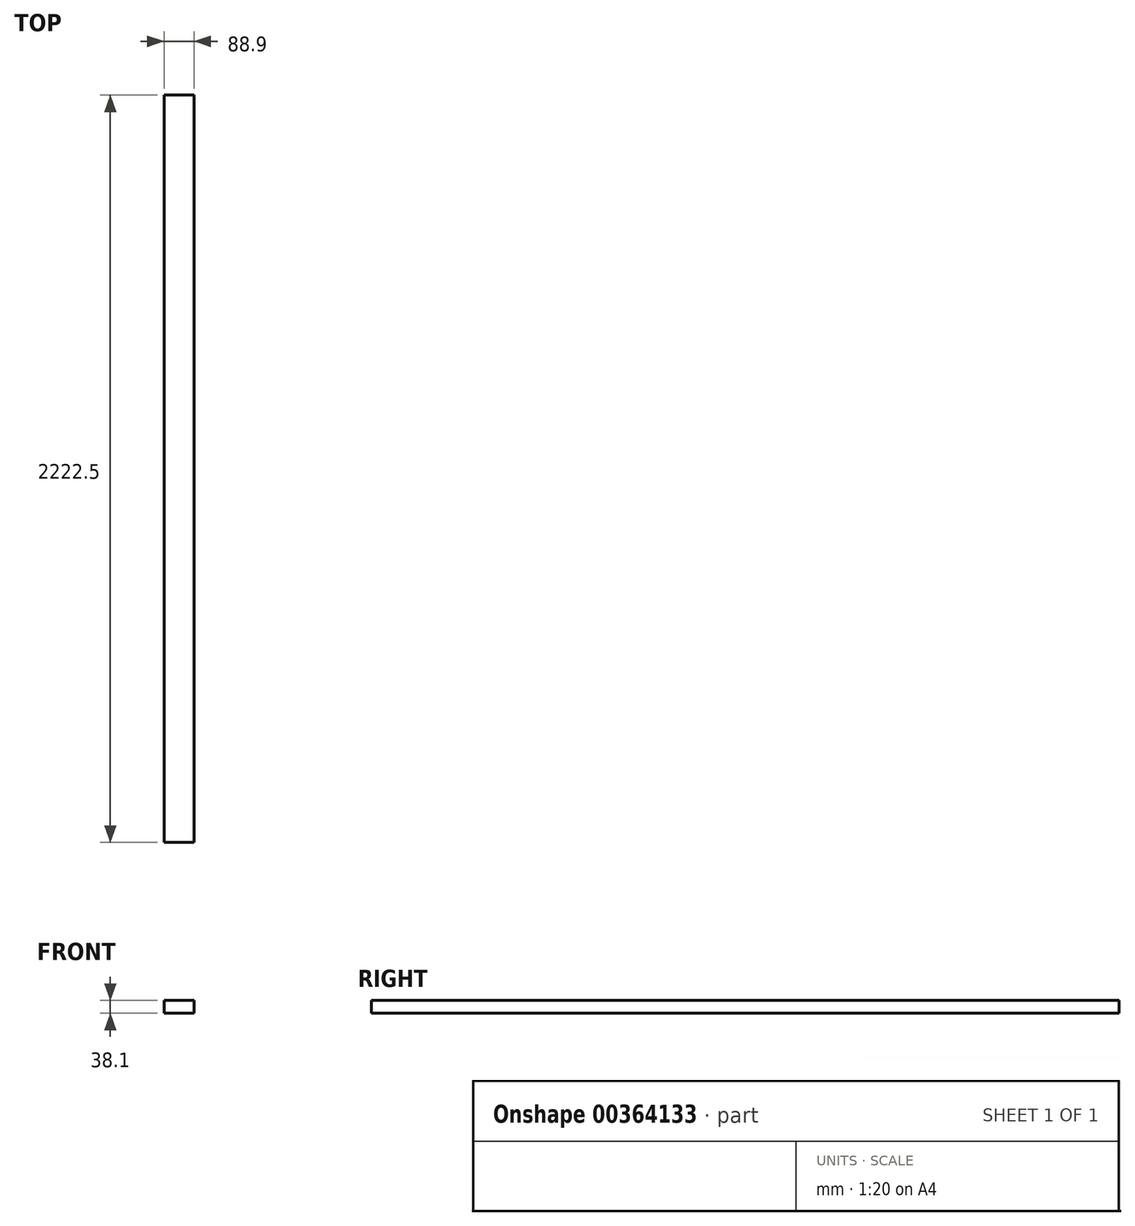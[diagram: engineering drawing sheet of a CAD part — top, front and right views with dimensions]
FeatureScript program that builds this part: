
annotation { "Feature Type Name" : "Feature", "Feature Type Description" : "" }
export const myFeature = defineFeature(function(context is Context, id is Id, definition is map)
    precondition{}
    {
        {
            var Q0;
            Q0=qCreatedBy(makeId("Front.planeOp"),FACE);
            var sketch = newSketch(context, id + "F0", { "sketchPlane" : qUnion([Q0])});
            skLineSegment(sketch, "E0.bottom", {"start": v(-37.78, 38.1) * mm, "end": v(51.12, 38.1) * mm});
            skLineSegment(sketch, "E0.top", {"start": v(-37.78, 0) * mm, "end": v(51.12, 0) * mm});
            skLineSegment(sketch, "E0.left", {"start": v(-37.78, 38.1) * mm, "end": v(-37.78, 0) * mm});
            skLineSegment(sketch, "E0.right", {"start": v(51.12, 38.1) * mm, "end": v(51.12, 0) * mm});
            skSolve(sketch);
        }
        {
            var Q0;
            Q0=makeQuery(id+"F0.imprint","IMPRINT",FACE,{"disambiguationData":[TD([[makeQuery(id+"F0.imprint","IMPRINT",EDGE,{"derivedFrom":sQuery(id+"F0.wireOp",EDGE,"E0.bottom")}),-1.0]])]});
            extrude(context, id + "F1", {"entities" : qUnion([Q0]), "depth" : 2222.5 * mm});
        }
    });
